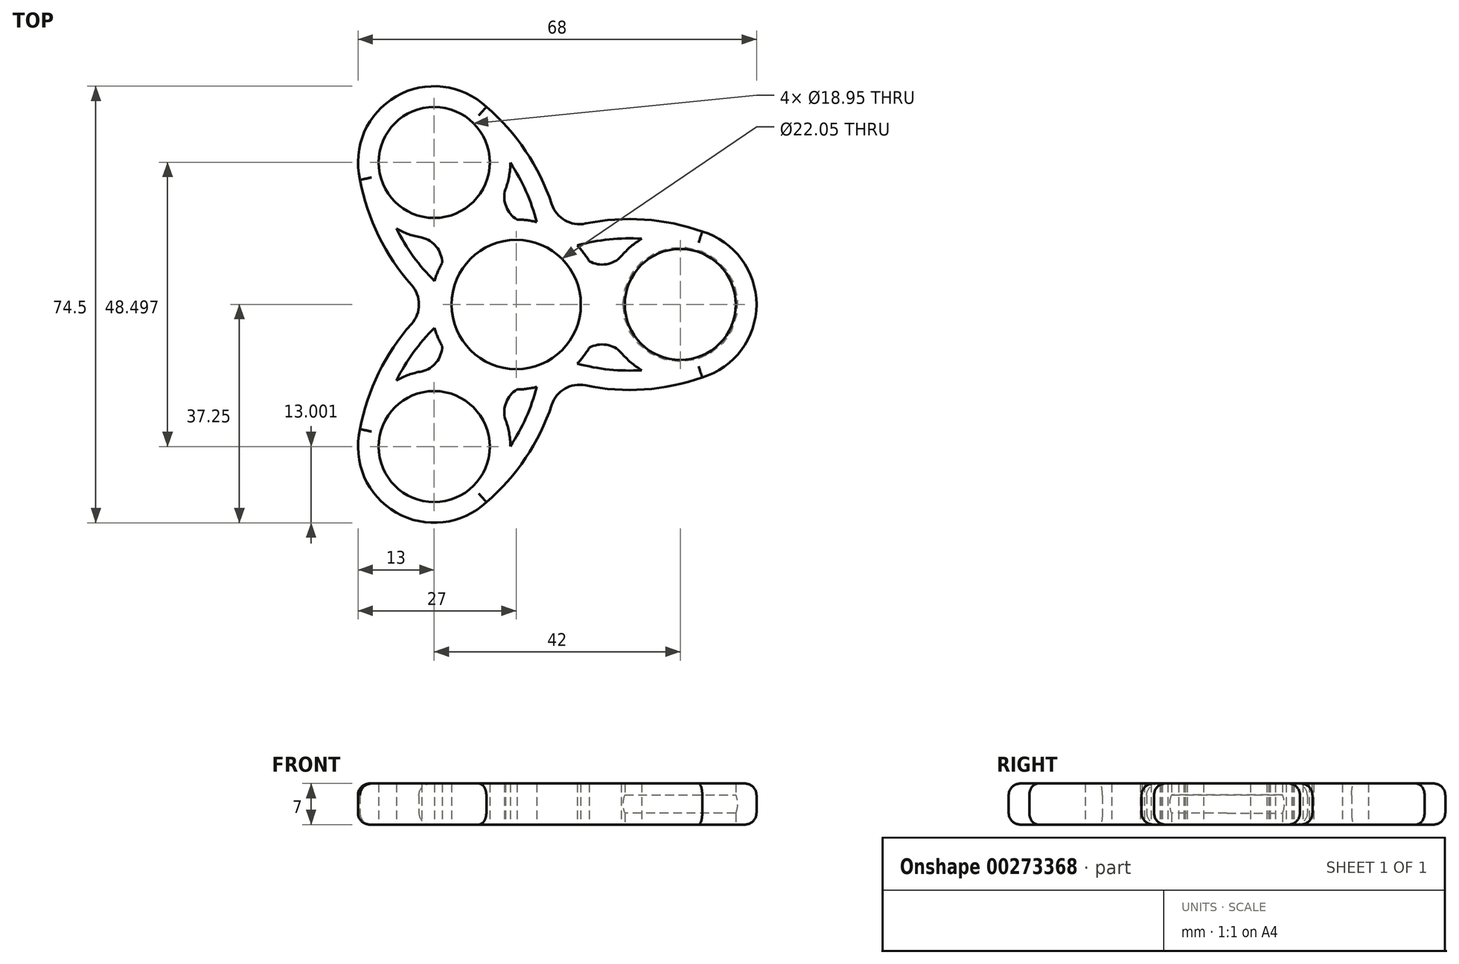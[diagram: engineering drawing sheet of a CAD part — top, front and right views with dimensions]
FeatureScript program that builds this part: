
annotation { "Feature Type Name" : "Feature", "Feature Type Description" : "" }
export const myFeature = defineFeature(function(context is Context, id is Id, definition is map)
    precondition{}
    {
        {
            var Q0;
            Q0=qCreatedBy(makeId("Top.planeOp"),FACE);
            var sketch = newSketch(context, id + "F0", { "sketchPlane" : qUnion([Q0])});
            skCircle(sketch, "E0", {"center": v(0, 0) * mm, "radius": 11.03 * mm});
            skCircle(sketch, "E1.2.0", {"center": v(-14, -24.25) * mm, "radius": 9.47 * mm});
            skArc(sketch, "E2", {"start": v(-26.65, -21.27) * mm, "mid": v(-20.5, -35.5) * mm, "end": v(-5.1, -33.72) * mm});
            skArc(sketch, "E3", {"start": v(-13.94, -3.98) * mm, "mid": v(-13.38, -5.6) * mm, "end": v(-12.63, -7.12) * mm});
            skLineSegment(sketch, "E4", {"start": v(-14, -24.25) * mm, "end": v(-14, -11.25) * mm, "construction": true});
            skLineSegment(sketch, "E5", {"start": v(-14, -24.25) * mm, "end": v(-23.2, -15.06) * mm, "construction": true});
            skArc(sketch, "E6", {"start": v(-17.87, -3.33) * mm, "mid": v(-23.49, -11.7) * mm, "end": v(-26.65, -21.27) * mm});
            skArc(sketch, "E7.0", {"start": v(-13.94, -3.98) * mm, "mid": v(-17.55, -8.2) * mm, "end": v(-20.43, -12.95) * mm});
            skArc(sketch, "E8", {"start": v(-16.1, -11.42) * mm, "mid": v(-13.64, -9.86) * mm, "end": v(-12.63, -7.12) * mm});
            skLineSegment(sketch, "E9", {"start": v(0, 0) * mm, "end": v(-14, -24.25) * mm, "construction": true});
            skArc(sketch, "E10.MirrorCS", {"start": v(-1.84, -19.66) * mm, "mid": v(-1.72, -16.74) * mm, "end": v(0.15, -14.5) * mm});
            skArc(sketch, "E11.MirrorCS", {"start": v(3.52, -14.07) * mm, "mid": v(1.68, -19.3) * mm, "end": v(-1, -24.17) * mm});
            skArc(sketch, "E12.MirrorCS", {"start": v(6.05, -17.14) * mm, "mid": v(1.62, -26.19) * mm, "end": v(-5.1, -33.72) * mm});
            skArc(sketch, "E13.trimOffspring", {"start": v(0.15, -14.5) * mm, "mid": v(1.85, -14.38) * mm, "end": v(3.52, -14.07) * mm});
            skArc(sketch, "E14.trimOffspring", {"start": v(-14, -11.25) * mm, "mid": v(-17.32, -11.68) * mm, "end": v(-20.43, -12.95) * mm});
            skArc(sketch, "E15.trimOffspring", {"start": v(-1, -24.17) * mm, "mid": v(-1.22, -21.88) * mm, "end": v(-1.84, -19.66) * mm});
            skArc(sketch, "E16.trimOffspring", {"start": v(10.42, -10.08) * mm, "mid": v(11.53, -8.8) * mm, "end": v(12.48, -7.38) * mm});
            skArc(sketch, "E17.1.1", {"start": v(31.75, -12.45) * mm, "mid": v(41, 0) * mm, "end": v(31.75, 12.45) * mm});
            skArc(sketch, "E17.1.2", {"start": v(17.95, 8.24) * mm, "mid": v(15.36, 6.88) * mm, "end": v(12.48, 7.38) * mm});
            skLineSegment(sketch, "E17.1.3", {"start": v(28, 0) * mm, "end": v(16.74, -6.5) * mm, "construction": true});
            skLineSegment(sketch, "E17.1.4", {"start": v(28, 0) * mm, "end": v(24.64, -12.56) * mm, "construction": true});
            skCircle(sketch, "E17.1.5", {"center": v(28, 0) * mm, "radius": 9.47 * mm});
            skArc(sketch, "E17.1.7", {"start": v(10.42, -10.08) * mm, "mid": v(15.88, -11.1) * mm, "end": v(21.43, -11.22) * mm});
            skArc(sketch, "E17.1.8", {"start": v(11.81, -13.8) * mm, "mid": v(21.87, -14.5) * mm, "end": v(31.75, -12.45) * mm});
            skArc(sketch, "E17.1.9", {"start": v(21.43, 11.22) * mm, "mid": v(19.55, 9.88) * mm, "end": v(17.95, 8.24) * mm});
            skArc(sketch, "E17.1.10", {"start": v(10.42, 10.08) * mm, "mid": v(15.88, 11.1) * mm, "end": v(21.43, 11.22) * mm});
            skArc(sketch, "E17.1.11", {"start": v(17.95, -8.24) * mm, "mid": v(15.36, -6.88) * mm, "end": v(12.48, -7.38) * mm});
            skArc(sketch, "E17.1.12", {"start": v(16.74, -6.5) * mm, "mid": v(18.78, -9.16) * mm, "end": v(21.43, -11.22) * mm});
            skLineSegment(sketch, "E17.1.13", {"start": v(0, 0) * mm, "end": v(28, 0) * mm, "construction": true});
            skArc(sketch, "E17.1.14", {"start": v(12.48, 7.38) * mm, "mid": v(11.53, 8.8) * mm, "end": v(10.42, 10.08) * mm});
            skArc(sketch, "E17.1.15", {"start": v(11.81, 13.8) * mm, "mid": v(21.87, 14.5) * mm, "end": v(31.75, 12.45) * mm});
            skArc(sketch, "E17.2.0", {"start": v(3.52, 14.07) * mm, "mid": v(1.85, 14.38) * mm, "end": v(0.15, 14.5) * mm});
            skArc(sketch, "E17.2.1", {"start": v(-5.1, 33.72) * mm, "mid": v(-20.5, 35.5) * mm, "end": v(-26.65, 21.27) * mm});
            skArc(sketch, "E17.2.2", {"start": v(-16.1, 11.42) * mm, "mid": v(-13.64, 9.86) * mm, "end": v(-12.63, 7.12) * mm});
            skLineSegment(sketch, "E17.2.3", {"start": v(-14, 24.25) * mm, "end": v(-2.74, 17.75) * mm, "construction": true});
            skLineSegment(sketch, "E17.2.4", {"start": v(-14, 24.25) * mm, "end": v(-1.44, 27.61) * mm, "construction": true});
            skCircle(sketch, "E17.2.5", {"center": v(-14, 24.25) * mm, "radius": 9.47 * mm});
            skArc(sketch, "E17.2.7", {"start": v(3.52, 14.07) * mm, "mid": v(1.68, 19.3) * mm, "end": v(-1, 24.17) * mm});
            skArc(sketch, "E17.2.8", {"start": v(6.05, 17.14) * mm, "mid": v(1.62, 26.19) * mm, "end": v(-5.1, 33.72) * mm});
            skArc(sketch, "E17.2.9", {"start": v(-20.43, 12.95) * mm, "mid": v(-18.34, 12) * mm, "end": v(-16.1, 11.42) * mm});
            skArc(sketch, "E17.2.10", {"start": v(-13.94, 3.98) * mm, "mid": v(-17.55, 8.2) * mm, "end": v(-20.43, 12.95) * mm});
            skArc(sketch, "E17.2.11", {"start": v(-1.84, 19.66) * mm, "mid": v(-1.72, 16.74) * mm, "end": v(0.15, 14.5) * mm});
            skArc(sketch, "E17.2.12", {"start": v(-2.74, 17.75) * mm, "mid": v(-1.45, 20.84) * mm, "end": v(-1, 24.17) * mm});
            skLineSegment(sketch, "E17.2.13", {"start": v(0, 0) * mm, "end": v(-14, 24.25) * mm, "construction": true});
            skArc(sketch, "E17.2.14", {"start": v(-12.63, 7.12) * mm, "mid": v(-13.38, 5.6) * mm, "end": v(-13.94, 3.98) * mm});
            skArc(sketch, "E17.2.15", {"start": v(-17.87, 3.33) * mm, "mid": v(-23.49, 11.7) * mm, "end": v(-26.65, 21.27) * mm});
            skPoint(sketch, "E18.visualSharp", {"position": v(7.25, -12.56) * mm});
            skArc(sketch, "E18.filletArc", {"start": v(11.81, -13.8) * mm, "mid": v(8.3, -14.38) * mm, "end": v(6.05, -17.14) * mm});
            skPoint(sketch, "E19.visualSharp", {"position": v(-14.5, 0) * mm});
            skArc(sketch, "E19.filletArc", {"start": v(-17.87, -3.33) * mm, "mid": v(-16.6, 0) * mm, "end": v(-17.87, 3.33) * mm});
            skPoint(sketch, "E20.visualSharp", {"position": v(7.25, 12.56) * mm});
            skArc(sketch, "E20.filletArc", {"start": v(6.05, 17.14) * mm, "mid": v(8.3, 14.38) * mm, "end": v(11.81, 13.8) * mm});
            skSolve(sketch);
        }
        {
            var Q0;
            Q0=makeQuery(id+"F0.imprint","IMPRINT",FACE,{"disambiguationData":[TD([[makeQuery(id+"F0.imprint","IMPRINT",EDGE,{"derivedFrom":sQuery(id+"F0.wireOp",EDGE,"E0")}),-1.0]])]});
            extrude(context, id + "F1", {"entities" : qUnion([Q0]), "depth" : 7 * mm});
        }
        {
            var Q0;
            Q0=makeQuery(id+"F1.opExtrude","CAP_EDGE",EDGE,{"disambiguationData":[OSD([sQuery(id+"F0.wireOp",EDGE,"E17.2.15")])],"isStart":false});
            var Q1;
            Q1=makeQuery(id+"F1.opExtrude","CAP_EDGE",EDGE,{"disambiguationData":[OSD([sQuery(id+"F0.wireOp",EDGE,"E17.2.15")])],"isStart":true});
            var Q2;
            Q2=makeQuery(id+"F1.opExtrude","CAP_EDGE",EDGE,{"disambiguationData":[OSD([sQuery(id+"F0.wireOp",EDGE,"E17.2.8")])],"isStart":false});
            var Q3;
            Q3=makeQuery(id+"F1.opExtrude","CAP_EDGE",EDGE,{"disambiguationData":[OSD([sQuery(id+"F0.wireOp",EDGE,"E17.1.15")])],"isStart":false});
            var Q4;
            Q4=makeQuery(id+"F1.opExtrude","CAP_EDGE",EDGE,{"disambiguationData":[OSD([sQuery(id+"F0.wireOp",EDGE,"E17.1.8")])],"isStart":false});
            var Q5;
            Q5=makeQuery(id+"F1.opExtrude","CAP_EDGE",EDGE,{"disambiguationData":[OSD([sQuery(id+"F0.wireOp",EDGE,"E12.MirrorCS")])],"isStart":false});
            var Q6;
            Q6=makeQuery(id+"F1.opExtrude","CAP_EDGE",EDGE,{"disambiguationData":[OSD([sQuery(id+"F0.wireOp",EDGE,"E6")])],"isStart":false});
            var Q7;
            Q7=makeQuery(id+"F1.opExtrude","CAP_EDGE",EDGE,{"disambiguationData":[OSD([sQuery(id+"F0.wireOp",EDGE,"E17.2.1")])],"isStart":false});
            var Q8;
            Q8=makeQuery(id+"F1.opExtrude","CAP_EDGE",EDGE,{"disambiguationData":[OSD([sQuery(id+"F0.wireOp",EDGE,"E17.2.1")])],"isStart":true});
            var Q9;
            Q9=makeQuery(id+"F1.opExtrude","CAP_EDGE",EDGE,{"disambiguationData":[OSD([sQuery(id+"F0.wireOp",EDGE,"E6")])],"isStart":true});
            var Q10;
            Q10=makeQuery(id+"F1.opExtrude","CAP_EDGE",EDGE,{"disambiguationData":[OSD([sQuery(id+"F0.wireOp",EDGE,"E2")])],"isStart":true});
            var Q11;
            Q11=makeQuery(id+"F1.opExtrude","CAP_EDGE",EDGE,{"disambiguationData":[OSD([sQuery(id+"F0.wireOp",EDGE,"E2")])],"isStart":false});
            var Q12;
            Q12=makeQuery(id+"F1.opExtrude","CAP_EDGE",EDGE,{"disambiguationData":[OSD([sQuery(id+"F0.wireOp",EDGE,"E17.1.1")])],"isStart":false});
            var Q13;
            Q13=makeQuery(id+"F1.opExtrude","CAP_EDGE",EDGE,{"disambiguationData":[OSD([sQuery(id+"F0.wireOp",EDGE,"E17.1.8")])],"isStart":true});
            var Q14;
            Q14=makeQuery(id+"F1.opExtrude","CAP_EDGE",EDGE,{"disambiguationData":[OSD([sQuery(id+"F0.wireOp",EDGE,"E17.1.1")])],"isStart":true});
            var Q15;
            Q15=makeQuery(id+"F1.opExtrude","CAP_EDGE",EDGE,{"disambiguationData":[OSD([sQuery(id+"F0.wireOp",EDGE,"E17.1.15")])],"isStart":true});
            fillet(context, id + "F2", {"entities" : qUnion([Q0, Q1, Q2, Q3, Q4, Q5, Q6, Q7, Q8, Q9, Q10, Q11, Q12, Q13, Q14, Q15]), "radius" : 2 * mm, "tangentPropagation" : true, "allowEdgeOverflow" : false});
        }
        {
            var Q0;
            Q0=qCreatedBy(makeId("Front.planeOp"),FACE);
            var sketch = newSketch(context, id + "F3", { "sketchPlane" : qUnion([Q0])});
            skLineSegment(sketch, "E21", {"start": v(0, 0) * mm, "end": v(0, 3.5) * mm, "construction": true});
            skLineSegment(sketch, "E22", {"start": v(0, 3.5) * mm, "end": v(22.2, 3.5) * mm, "construction": true});
            skCircle(sketch, "E23", {"center": v(22.2, 3.5) * mm, "radius": 4 * mm});
            skLineSegment(sketch, "E24", {"start": v(0, 3.5) * mm, "end": v(28, 3.5) * mm, "construction": true});
            skLineSegment(sketch, "E25", {"start": v(28, 7.15) * mm, "end": v(28, -0.55) * mm});
            skCircle(sketch, "E26", {"center": v(28, 3.5) * mm, "radius": 9.53 * mm, "construction": true});
            skSolve(sketch);
        }
        {
            var Q0;
            Q0=makeQuery(id+"F3.imprint","IMPRINT",FACE,{"disambiguationData":[TD([[makeQuery(id+"F3.imprint","IMPRINT",EDGE,{"derivedFrom":sQuery(id+"F3.wireOp",EDGE,"E23")}),1.0]])]});
            var Q1;
            Q1=sQuery(id+"F3.wireOp",EDGE,"E25");
            revolve(context, id + "F4", {"operationType" : NewBodyOperationType.REMOVE, "entities" : qUnion([Q0]), "axis" : qUnion([Q1]), "revolveType" : RevolveType.FULL, "oppositeDirection" : true});
        }
        {
            var Q0;
            Q0=qCreatedBy(makeId("Top.planeOp"),FACE);
            var sketch = newSketch(context, id + "F5", { "sketchPlane" : qUnion([Q0])});
            skLineSegment(sketch, "E27", {"start": v(0, 0) * mm, "end": v(-28.62, -49.57) * mm});
            skSolve(sketch);
        }
    });
